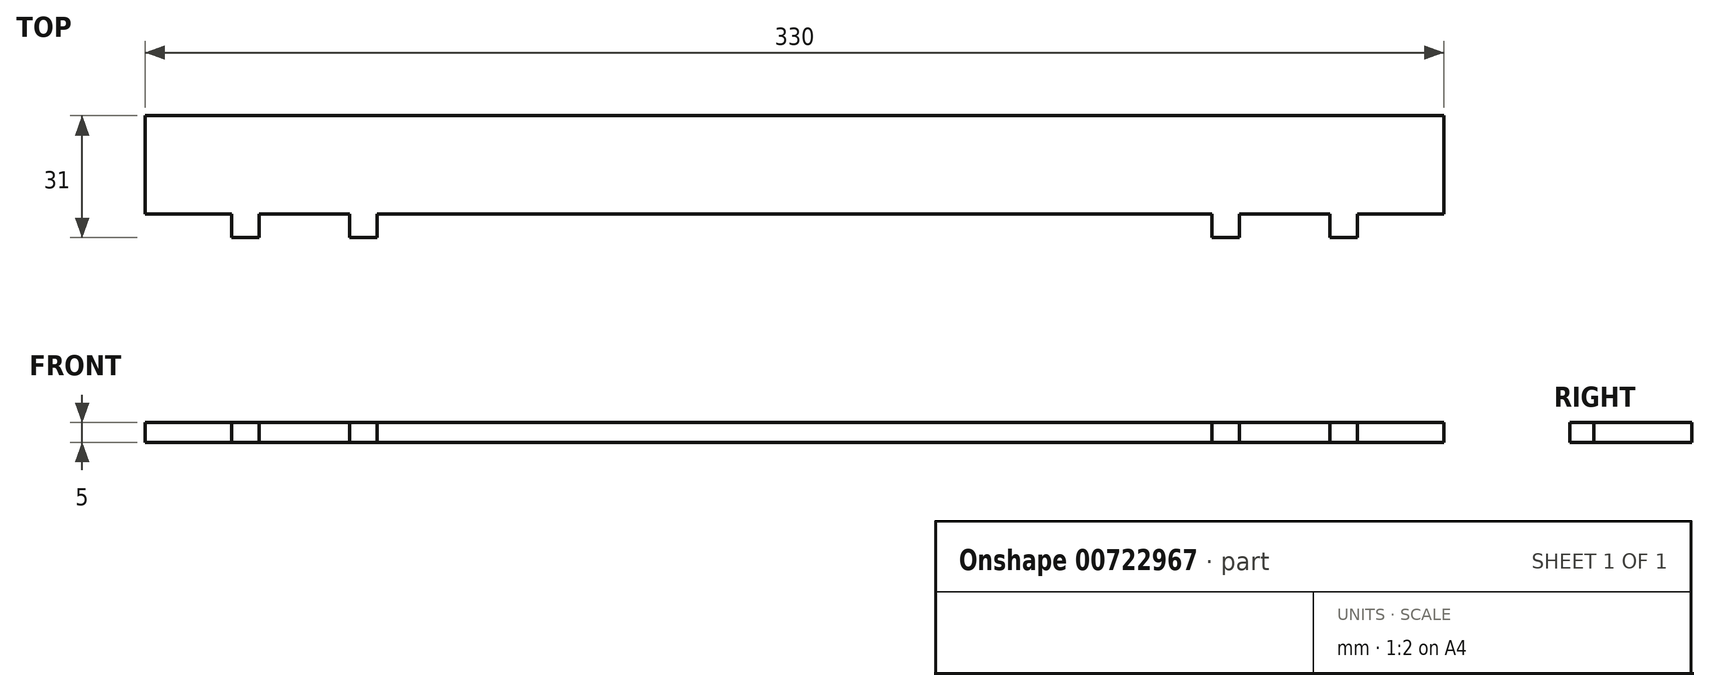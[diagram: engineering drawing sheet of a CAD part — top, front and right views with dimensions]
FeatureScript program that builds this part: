
annotation { "Feature Type Name" : "Feature", "Feature Type Description" : "" }
export const myFeature = defineFeature(function(context is Context, id is Id, definition is map)
    precondition{}
    {
        {
            var Q0;
            Q0=qCreatedBy(makeId("Top.planeOp"),FACE);
            var sketch = newSketch(context, id + "F0", { "sketchPlane" : qUnion([Q0])});
            skLineSegment(sketch, "E0", {"start": v(0, 0) * mm, "end": v(0, 25) * mm});
            skLineSegment(sketch, "E1", {"start": v(0, 25) * mm, "end": v(-165, 25) * mm});
            skLineSegment(sketch, "E2", {"start": v(-165, 25) * mm, "end": v(-165, 0) * mm});
            skLineSegment(sketch, "E3", {"start": v(-165, 0) * mm, "end": v(-143, 0) * mm});
            skLineSegment(sketch, "E4", {"start": v(-143, 0) * mm, "end": v(-143, -6) * mm});
            skLineSegment(sketch, "E5", {"start": v(-143, -6) * mm, "end": v(-136, -6) * mm});
            skLineSegment(sketch, "E6", {"start": v(-136, -6) * mm, "end": v(-136, 0) * mm});
            skLineSegment(sketch, "E7", {"start": v(-136, 0) * mm, "end": v(-113, 0) * mm});
            skLineSegment(sketch, "E8", {"start": v(-113, 0) * mm, "end": v(-113, -6) * mm});
            skLineSegment(sketch, "E9", {"start": v(-113, -6) * mm, "end": v(-106, -6) * mm});
            skLineSegment(sketch, "E10", {"start": v(-106, -6) * mm, "end": v(-106, 0) * mm});
            skLineSegment(sketch, "E11", {"start": v(-106, 0) * mm, "end": v(0, 0) * mm});
            skLineSegment(sketch, "E12", {"start": v(0, 0) * mm, "end": v(106, 0) * mm, "construction": true});
            skSolve(sketch);
        }
        {
            var Q0;
            Q0 = qSketchRegion(id + "F0", true);
            extrude(context, id + "F1", {"entities" : qUnion([Q0]), "depth" : 5 * mm, "offsetDistance" : 25 * mm});
        }
        {
            var Q0;
            Q0=makeQuery(id+"F1.opExtrude","SWEPT_BODY",BODY,{"disambiguationData":[OSD([sQuery(id+"F0.wireOp",EDGE,"E0"),sQuery(id+"F0.wireOp",EDGE,"E1"),sQuery(id+"F0.wireOp",EDGE,"E2"),sQuery(id+"F0.wireOp",EDGE,"E3"),sQuery(id+"F0.wireOp",EDGE,"E4"),sQuery(id+"F0.wireOp",EDGE,"E5"),sQuery(id+"F0.wireOp",EDGE,"E6"),sQuery(id+"F0.wireOp",EDGE,"E7"),sQuery(id+"F0.wireOp",EDGE,"E8"),sQuery(id+"F0.wireOp",EDGE,"E9"),sQuery(id+"F0.wireOp",EDGE,"E10"),sQuery(id+"F0.wireOp",EDGE,"E11")])]});
            var Q1;
            Q1=makeQuery(id+"F1.opExtrude","SWEPT_FACE",FACE,{"disambiguationData":[OSD([sQuery(id+"F0.wireOp",EDGE,"E0")])]});
            mirror(context, id + "F2", {"operationType" : NewBodyOperationType.ADD, "entities" : qUnion([Q0]), "mirrorPlane" : qUnion([Q1])});
        }
    });
